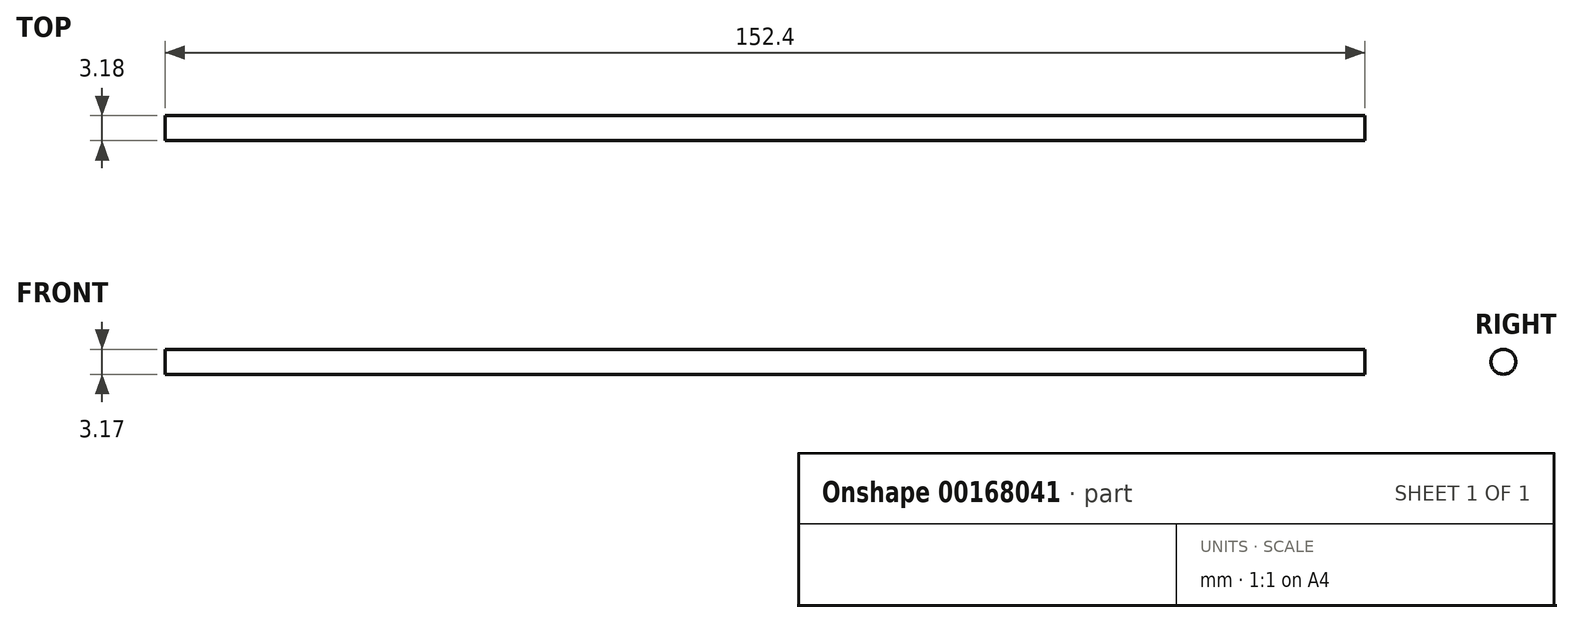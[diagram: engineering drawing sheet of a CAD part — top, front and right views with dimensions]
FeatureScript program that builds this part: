
annotation { "Feature Type Name" : "Feature", "Feature Type Description" : "" }
export const myFeature = defineFeature(function(context is Context, id is Id, definition is map)
    precondition{}
    {
        {
            var Q0;
            Q0=qCreatedBy(makeId("Right.planeOp"),FACE);
            var sketch = newSketch(context, id + "F0", { "sketchPlane" : qUnion([Q0])});
            skCircle(sketch, "E0", {"center": v(-39.27, 7.04) * mm, "radius": 1.59 * mm});
            skSolve(sketch);
        }
        {
            var Q0;
            Q0 = qSketchRegion(id + "F0", true);
            extrude(context, id + "F1", {"entities" : qUnion([Q0]), "depth" : 152.4 * mm});
        }
    });
